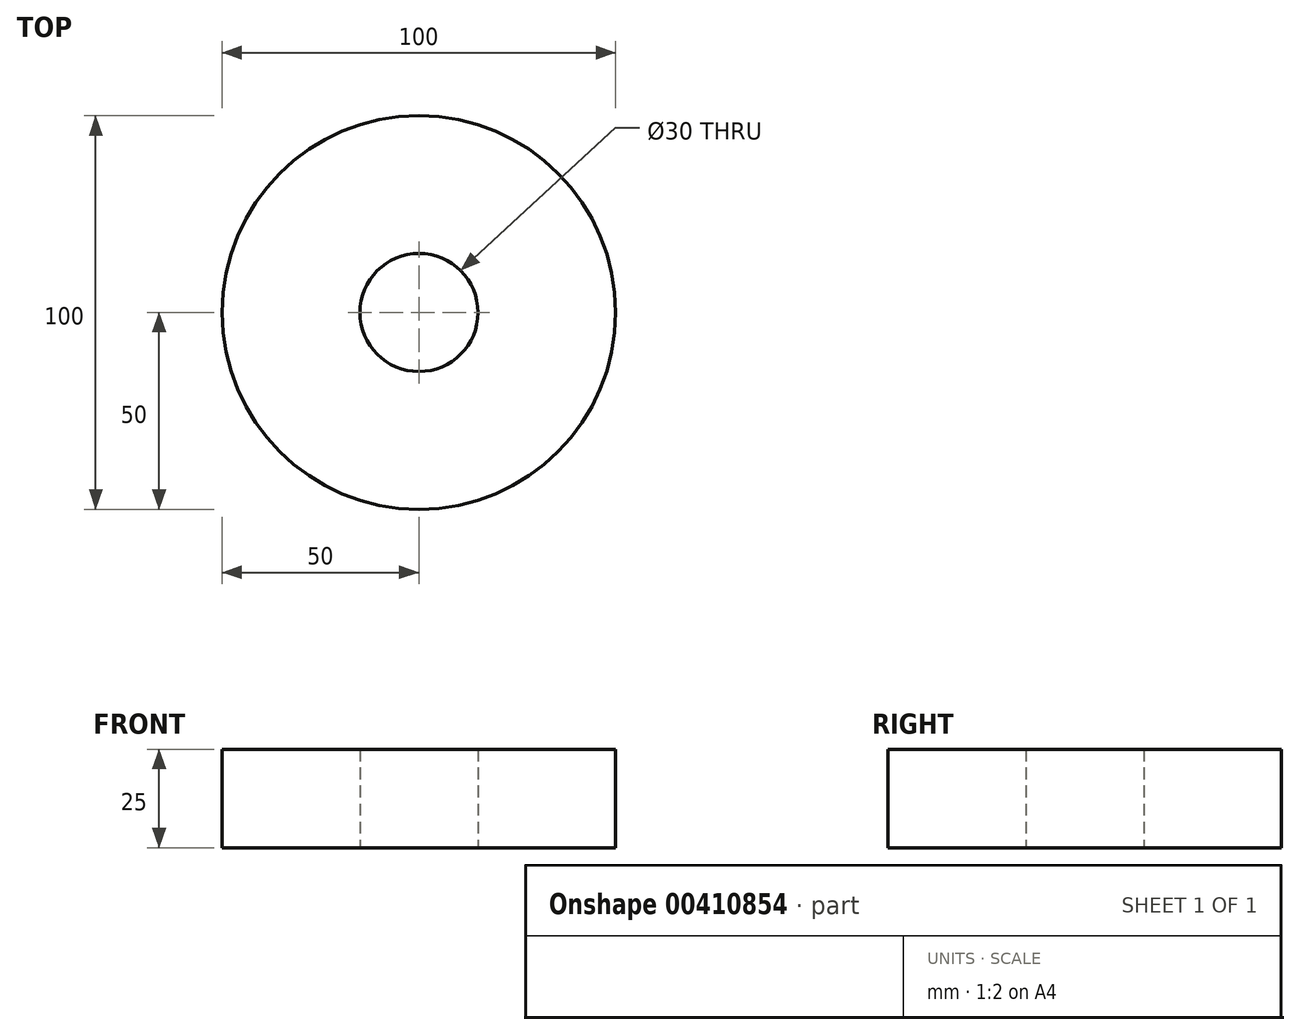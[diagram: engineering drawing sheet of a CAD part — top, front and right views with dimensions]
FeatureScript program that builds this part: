
annotation { "Feature Type Name" : "Feature", "Feature Type Description" : "" }
export const myFeature = defineFeature(function(context is Context, id is Id, definition is map)
    precondition{}
    {
        {
            var Q0;
            Q0=qCreatedBy(makeId("Top.planeOp"),FACE);
            var sketch = newSketch(context, id + "F0", { "sketchPlane" : qUnion([Q0])});
            skCircle(sketch, "E0", {"center": v(0, 0) * mm, "radius": 50 * mm});
            skCircle(sketch, "E1", {"center": v(0, 0) * mm, "radius": 15 * mm});
            skSolve(sketch);
        }
        {
            var Q0;
            Q0 = qSketchRegion(id + "F0", true);
            extrude(context, id + "F1", {"entities" : qUnion([Q0]), "depth" : 25 * mm});
        }
    });
